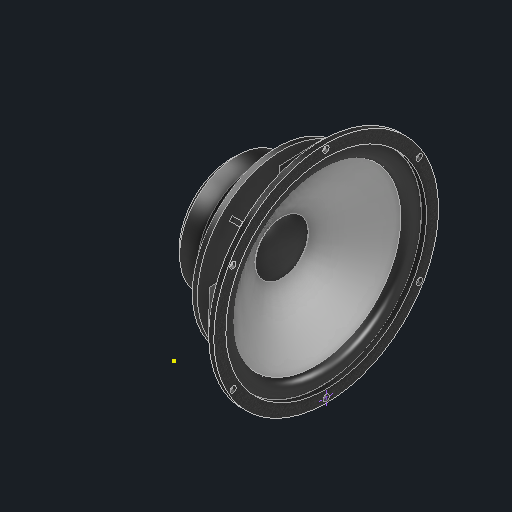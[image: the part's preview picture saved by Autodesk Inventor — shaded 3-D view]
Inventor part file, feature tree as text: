
AUTODESK INVENTOR PART (.ipt)
format: ipt  version: 2022 (Build 260153070, 153G)  size: 559,104 bytes
history: native  units: mm
features: sketch x6, hole x2, pattern_circular x2, other x1, revolve x1, extrude x1
ambient origin geometry x8: Origin, YZ Plane, XZ Plane, XY Plane, X Axis, Y Axis, Z Axis, Center Point
bodies: Body1 (feature_tree)
feature tree (13):
  other  "Твердое тело1"
  revolve  "Вращение1"
  sketch  "Эскиз2"
  sketch  "Эскиз3"
  hole  "Отверстие1"  [1 undecoded]
  pattern_circular  "Круговой массив1"  [2 undecoded]
  hole  "Отверстие2"  [1 undecoded]
  sketch  "Эскиз5"
  extrude  "Выдавливание1"  TaperAngle=360.0deg  [1 undecoded]
  pattern_circular  "Круговой массив2"  Count=6 Angle=360.0deg
  sketch  "Эскиз1"
  sketch  "Эскиз4"
  sketch  "Эскиз6"
note: 5 required parameter values undecoded (feature->parameter linkage not recoverable at this tier; creation-order binding heuristic only, values carry confidence <= 0.55)
